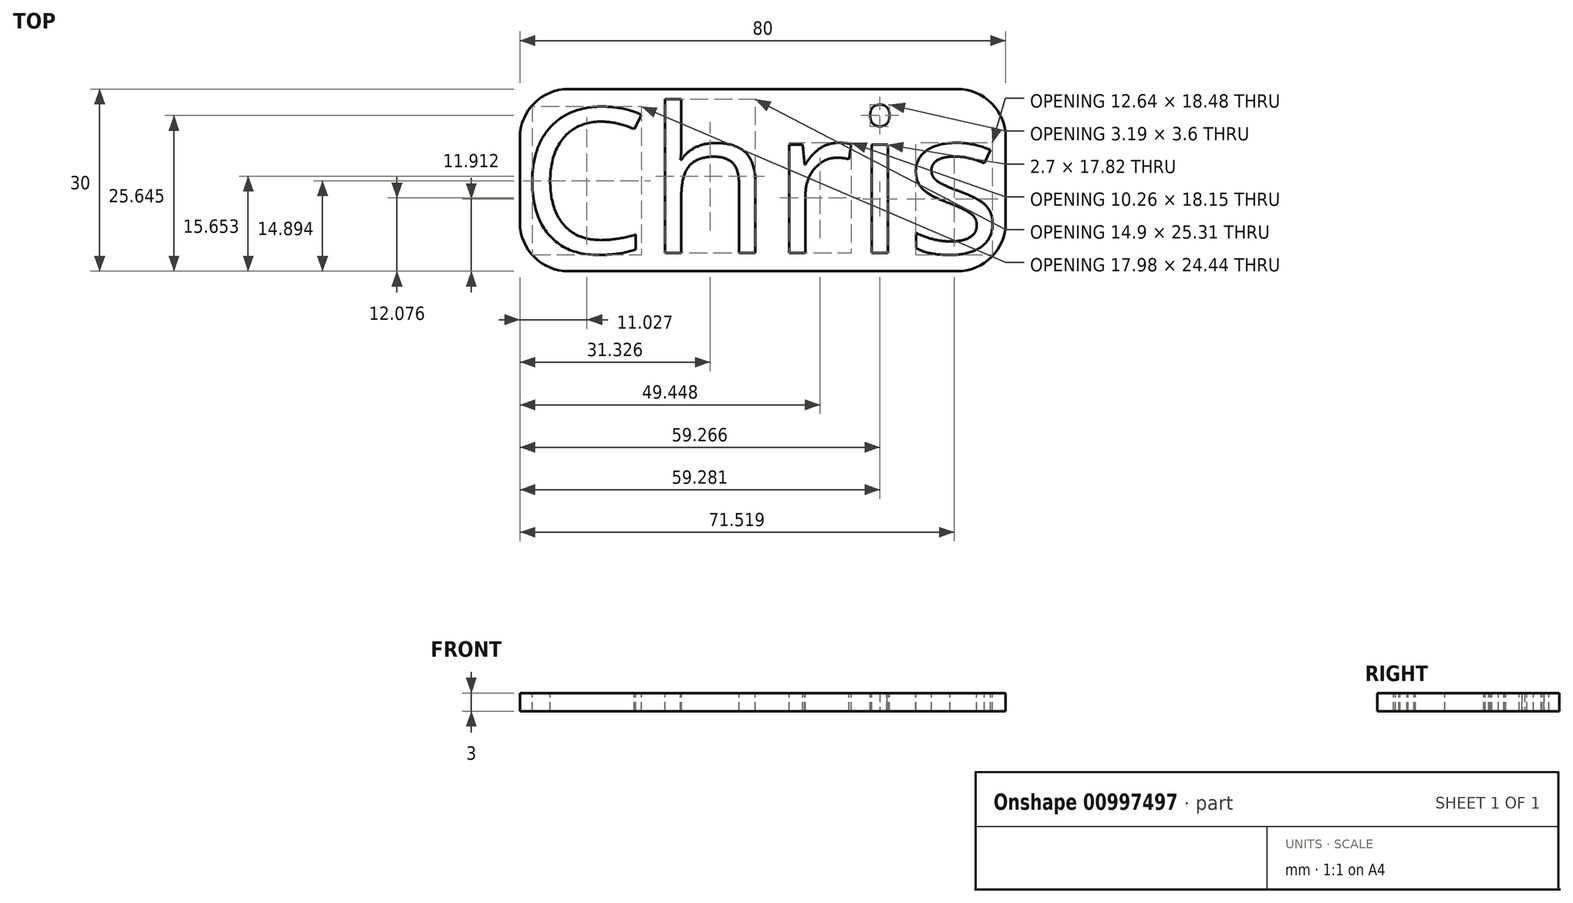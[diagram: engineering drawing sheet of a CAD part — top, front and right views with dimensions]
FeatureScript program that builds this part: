
annotation { "Feature Type Name" : "Feature", "Feature Type Description" : "" }
export const myFeature = defineFeature(function(context is Context, id is Id, definition is map)
    precondition{}
    {
        {
            var Q0;
            Q0=qCreatedBy(makeId("Top.planeOp"),FACE);
            var sketch = newSketch(context, id + "F0", { "sketchPlane" : qUnion([Q0])});
            skLineSegment(sketch, "E0.bottom", {"start": v(0, 0) * mm, "end": v(80, 0) * mm});
            skLineSegment(sketch, "E0.top", {"start": v(0, 30) * mm, "end": v(80, 30) * mm});
            skLineSegment(sketch, "E0.left", {"start": v(0, 0) * mm, "end": v(0, 30) * mm});
            skLineSegment(sketch, "E0.right", {"start": v(80, 0) * mm, "end": v(80, 30) * mm});
            skText(sketch, "E1", { "text": "Chris", "fontName": "OpenSans-Regular.ttf"});
            skLineSegment(sketch, "E2", {"start": v(0, 15) * mm, "end": v(80, 15) * mm, "construction": true});
            const initialGuessF0  = {"E1": [0, 0.003, 1, 0, 0.02398]};
            skSetInitialGuess(sketch, initialGuessF0);
            skSolve(sketch);
        }
        {
            var Q0;
            Q0 = qSketchRegion(id + "F0", true);
            extrude(context, id + "F1", {"entities" : qUnion([Q0]), "oppositeDirection" : true, "depth" : 3 * mm, "offsetDistance" : 25 * mm});
        }
        {
            var Q0;
            Q0=makeQuery(id+"F1.opExtrude","SWEPT_EDGE",EDGE,{"disambiguationData":[OSD([sQuery(id+"F0.wireOp",EDGE,"E0.top"),sQuery(id+"F0.wireOp",EDGE,"E0.left")])]});
            var Q1;
            Q1=makeQuery(id+"F1.opExtrude","SWEPT_EDGE",EDGE,{"disambiguationData":[OSD([sQuery(id+"F0.wireOp",EDGE,"E0.bottom"),sQuery(id+"F0.wireOp",EDGE,"E0.left")])]});
            var Q2;
            Q2=makeQuery(id+"F1.opExtrude","SWEPT_EDGE",EDGE,{"disambiguationData":[OSD([sQuery(id+"F0.wireOp",EDGE,"E0.top"),sQuery(id+"F0.wireOp",EDGE,"E0.right")])]});
            var Q3;
            Q3=makeQuery(id+"F1.opExtrude","SWEPT_EDGE",EDGE,{"disambiguationData":[OSD([sQuery(id+"F0.wireOp",EDGE,"E0.bottom"),sQuery(id+"F0.wireOp",EDGE,"E0.right")])]});
            fillet(context, id + "F2", {"entities" : qUnion([Q0, Q1, Q2, Q3]), "radius" : 8 * mm, "tangentPropagation" : true, "allowEdgeOverflow" : false});
        }
    });
